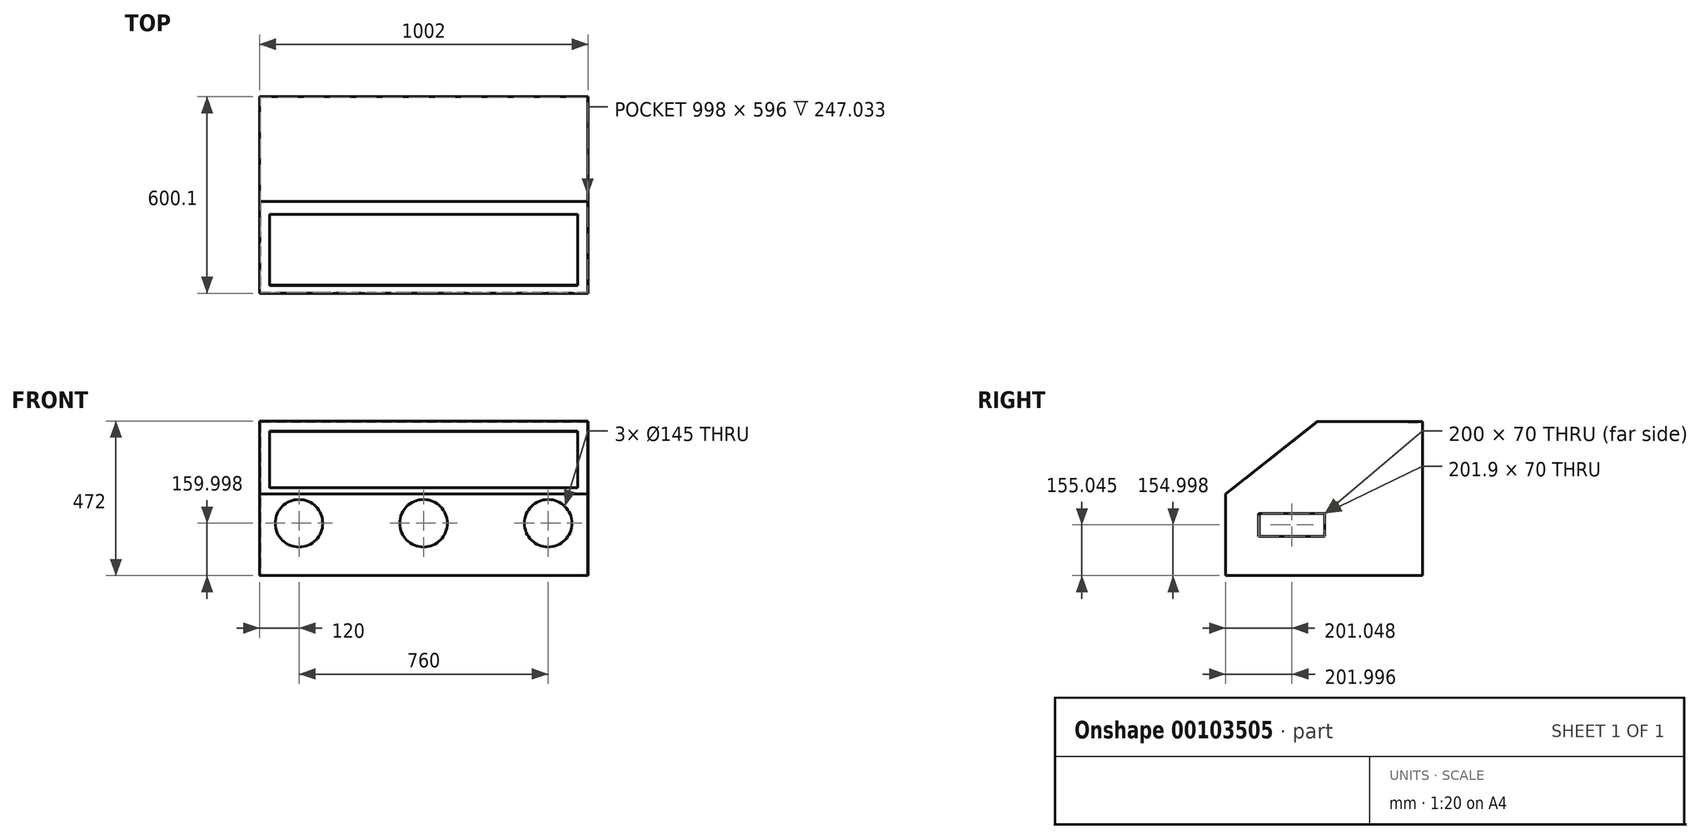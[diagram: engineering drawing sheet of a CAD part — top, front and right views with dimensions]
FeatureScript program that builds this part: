
annotation { "Feature Type Name" : "Feature", "Feature Type Description" : "" }
export const myFeature = defineFeature(function(context is Context, id is Id, definition is map)
    precondition{}
    {
        {
            var Q0;
            Q0=makeQuery(id+"F8.imprint","IMPRINT",FACE,{"disambiguationData":[TD([[makeQuery(id+"F8.imprint","IMPRINT",EDGE,{"derivedFrom":makeQuery(id+"F7.opExtrude","CAP_EDGE",EDGE,{"disambiguationData":[OSD([sQuery(id+"F1.wireOp",EDGE,"E6.0")])],"isStart":false})}),1.0]])]});
            var Q1;
            Q1=qCreatedBy(makeId("Right.planeOp"),FACE);
            cPlane(context, id + "F0", {"entities" : qUnion([Q0, Q1]), "cplaneType" : CPlaneType.OFFSET, "offset" : 1000 * mm, "width" : 150 * mm, "height" : 150 * mm});
        }
        {
            var Q0;
            Q0=qCreatedBy(makeId("Right.planeOp"),FACE);
            var sketch = newSketch(context, id + "F1", { "sketchPlane" : qUnion([Q0])});
            skLineSegment(sketch, "E0.top", {"start": v(-288.55, -222.8) * mm, "end": v(311.45, -222.8) * mm});
            skLineSegment(sketch, "E0.right", {"start": v(311.45, 247.2) * mm, "end": v(311.45, -222.8) * mm});
            skPoint(sketch, "E1", {"position": v(-288.55, 27.2) * mm});
            skPoint(sketch, "E2", {"position": v(-8.55, 249.2) * mm});
            skLineSegment(sketch, "E3", {"start": v(-8.55, 249.2) * mm, "end": v(-288.55, 27.2) * mm});
            skLineSegment(sketch, "E4", {"start": v(-8.55, 249.2) * mm, "end": v(311.45, 247.2) * mm});
            skLineSegment(sketch, "E5", {"start": v(-288.55, -222.8) * mm, "end": v(-288.55, 27.2) * mm});
            skLineSegment(sketch, "E6.0", {"start": v(-7.86, 247.2) * mm, "end": v(-286.55, 26.24) * mm});
            skLineSegment(sketch, "E6.1", {"start": v(-286.55, -220.8) * mm, "end": v(-286.55, 26.24) * mm});
            skLineSegment(sketch, "E6.2", {"start": v(-7.86, 247.2) * mm, "end": v(309.45, 245.22) * mm});
            skLineSegment(sketch, "E6.3", {"start": v(309.45, 245.22) * mm, "end": v(309.45, -220.8) * mm});
            skLineSegment(sketch, "E6.4", {"start": v(-286.55, -220.8) * mm, "end": v(309.45, -220.8) * mm});
            skLineSegment(sketch, "E7.bottom", {"start": v(-186.55, -32.8) * mm, "end": v(13.45, -32.8) * mm});
            skLineSegment(sketch, "E7.top", {"start": v(-186.55, -102.8) * mm, "end": v(13.45, -102.8) * mm});
            skLineSegment(sketch, "E7.left", {"start": v(-186.55, -32.8) * mm, "end": v(-186.55, -102.8) * mm});
            skLineSegment(sketch, "E7.right", {"start": v(13.45, -32.8) * mm, "end": v(13.45, -102.8) * mm});
            skSolve(sketch);
        }
        {
            var Q0;
            Q0=makeQuery(id+"F1.imprint","IMPRINT",FACE,{"disambiguationData":[TD([[makeQuery(id+"F1.imprint","IMPRINT",EDGE,{"derivedFrom":sQuery(id+"F1.wireOp",EDGE,"E0.top")}),1.0]])]});
            extrude(context, id + "F2", {"entities" : qUnion([Q0]), "depth" : 1000 * mm});
        }
        {
            var Q0;
            Q0=makeQuery(id+"F2.opExtrude","SWEPT_FACE",FACE,{"disambiguationData":[OSD([sQuery(id+"F1.wireOp",EDGE,"E3")])]});
            var sketch = newSketch(context, id + "F3", { "sketchPlane" : qUnion([Q0])});
            skLineSegment(sketch, "E8.bottom", {"start": v(30, 98.12) * mm, "end": v(970, 98.12) * mm});
            skLineSegment(sketch, "E8.top", {"start": v(30, -179.2) * mm, "end": v(970, -179.2) * mm});
            skLineSegment(sketch, "E8.left", {"start": v(30, 98.12) * mm, "end": v(30, -179.2) * mm});
            skLineSegment(sketch, "E8.right", {"start": v(970, 98.12) * mm, "end": v(970, -179.2) * mm});
            skSolve(sketch);
        }
        {
            var Q0;
            Q0=makeQuery(id+"F3.imprint","IMPRINT",FACE,{"disambiguationData":[TD([[makeQuery(id+"F3.imprint","IMPRINT",EDGE,{"derivedFrom":sQuery(id+"F3.wireOp",EDGE,"E8.bottom")}),-1.0]])]});
            extrude(context, id + "F4", {"entities" : qUnion([Q0]), "operationType" : NewBodyOperationType.REMOVE, "oppositeDirection" : true, "depth" : 5 * mm});
        }
        {
            var Q0;
            Q0=makeQuery(id+"F2.opExtrude","SWEPT_FACE",FACE,{"disambiguationData":[OSD([sQuery(id+"F1.wireOp",EDGE,"E5")])]});
            var sketch = newSketch(context, id + "F5", { "sketchPlane" : qUnion([Q0])});
            skPoint(sketch, "E9", {"position": v(120, -62.8) * mm});
            skPoint(sketch, "E10.1.0.0", {"position": v(500, -62.8) * mm});
            skPoint(sketch, "E10.2.0.0", {"position": v(880, -62.8) * mm});
            skLineSegment(sketch, "E10.direction1", {"start": v(120, -62.8) * mm, "end": v(500, -62.8) * mm, "construction": true});
            skSolve(sketch);
        }
        {
            var Q0;
            Q0=sQuery(id+"F5.wireOp",VERTEX,"E9");
            var Q1;
            Q1=sQuery(id+"F5.wireOp",VERTEX,"E10.1.0.0");
            var Q2;
            Q2=sQuery(id+"F5.wireOp",VERTEX,"E10.2.0.0");
            var Q3;
            Q3=makeQuery(id+"F2.opExtrude","SWEPT_BODY",BODY,{"disambiguationData":[OSD([sQuery(id+"F1.wireOp",EDGE,"E0.top"),sQuery(id+"F1.wireOp",EDGE,"E0.right"),sQuery(id+"F1.wireOp",EDGE,"E3"),sQuery(id+"F1.wireOp",EDGE,"E4"),sQuery(id+"F1.wireOp",EDGE,"E5"),sQuery(id+"F1.wireOp",EDGE,"E6.0"),sQuery(id+"F1.wireOp",EDGE,"E6.1"),sQuery(id+"F1.wireOp",EDGE,"E6.2"),sQuery(id+"F1.wireOp",EDGE,"E6.3"),sQuery(id+"F1.wireOp",EDGE,"E6.4")])]});
            hole(context, id + "F6", {"style" : HoleStyle.SIMPLE, "endStyle" : HoleEndStyle.BLIND, "holeDiameter" : 145 * mm, "holeDepth" : 4 * mm, "locations" : qUnion([Q0, Q1, Q2]), "scope" : qUnion([Q3])});
        }
        {
            var Q0;
            Q0=makeQuery(id+"F1.imprint","IMPRINT",FACE,{"disambiguationData":[TD([[makeQuery(id+"F1.imprint","IMPRINT",EDGE,{"derivedFrom":sQuery(id+"F1.wireOp",EDGE,"E6.0")}),1.0]])]});
            extrude(context, id + "F7", {"entities" : qUnion([Q0]), "operationType" : NewBodyOperationType.ADD, "depth" : 2 * mm});
        }
        {
            var Q0;
            Q0=qCreatedBy(id+"F0.planeOp",FACE);
            var sketch = newSketch(context, id + "F8", { "sketchPlane" : qUnion([Q0])});
            skLineSegment(sketch, "E11.top", {"start": v(-288.45, -222.75) * mm, "end": v(311.55, -222.75) * mm});
            skLineSegment(sketch, "E11.right", {"start": v(311.55, 247.25) * mm, "end": v(311.55, -222.75) * mm});
            skPoint(sketch, "E12", {"position": v(-288.45, 27.25) * mm});
            skPoint(sketch, "E13", {"position": v(-8.45, 247.25) * mm});
            skLineSegment(sketch, "E14", {"start": v(-8.45, 247.25) * mm, "end": v(-288.45, 27.25) * mm});
            skLineSegment(sketch, "E15", {"start": v(-8.45, 247.25) * mm, "end": v(311.55, 247.25) * mm});
            skLineSegment(sketch, "E16", {"start": v(-288.45, -222.75) * mm, "end": v(-288.45, 27.25) * mm});
            skLineSegment(sketch, "E17.bottom", {"start": v(-188.45, -32.75) * mm, "end": v(13.45, -32.75) * mm});
            skLineSegment(sketch, "E17.top", {"start": v(-188.45, -102.75) * mm, "end": v(13.45, -102.75) * mm});
            skLineSegment(sketch, "E17.left", {"start": v(-188.45, -32.75) * mm, "end": v(-188.45, -102.75) * mm});
            skLineSegment(sketch, "E17.right", {"start": v(13.45, -32.75) * mm, "end": v(13.45, -102.75) * mm});
            skSolve(sketch);
        }
        {
            var Q0;
            Q0=makeQuery(id+"F8.imprint","IMPRINT",FACE,{"disambiguationData":[TD([[makeQuery(id+"F8.imprint","IMPRINT",EDGE,{"derivedFrom":sQuery(id+"F8.wireOp",EDGE,"E11.top")}),1.0]])]});
            extrude(context, id + "F9", {"entities" : qUnion([Q0]), "operationType" : NewBodyOperationType.ADD, "depth" : 2 * mm});
        }
    });
